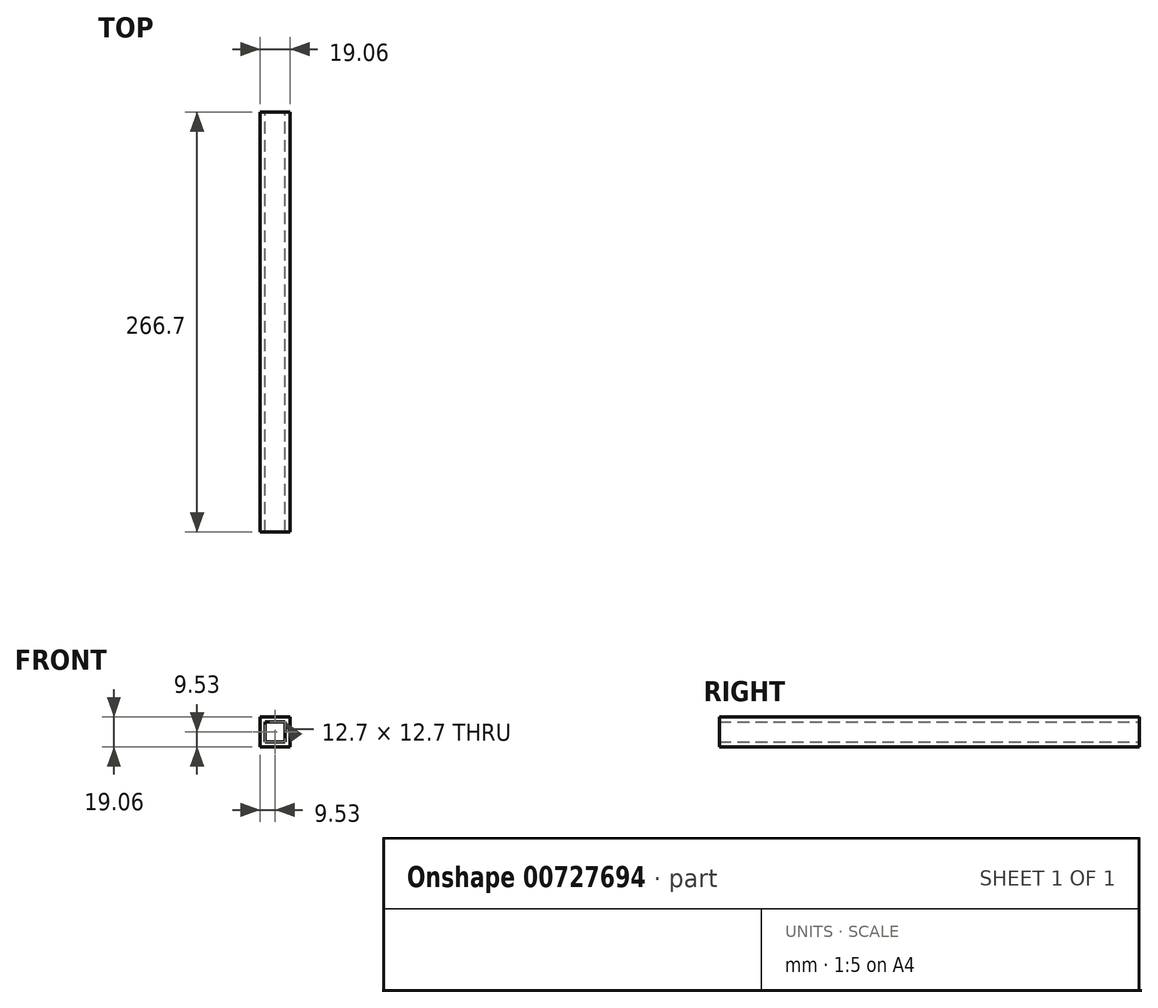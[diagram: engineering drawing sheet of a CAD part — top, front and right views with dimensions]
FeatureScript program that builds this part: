
annotation { "Feature Type Name" : "Feature", "Feature Type Description" : "" }
export const myFeature = defineFeature(function(context is Context, id is Id, definition is map)
    precondition{}
    {
        {
            var Q0;
            Q0=qCreatedBy(makeId("Front.planeOp"),FACE);
            var sketch = newSketch(context, id + "F0", { "sketchPlane" : qUnion([Q0])});
            skLineSegment(sketch, "E0.bottom", {"start": v(6.35, 6.35) * mm, "end": v(-6.35, 6.35) * mm});
            skLineSegment(sketch, "E0.top", {"start": v(6.35, -6.35) * mm, "end": v(-6.35, -6.35) * mm});
            skLineSegment(sketch, "E0.left", {"start": v(6.35, 6.35) * mm, "end": v(6.35, -6.35) * mm});
            skLineSegment(sketch, "E0.right", {"start": v(-6.35, 6.35) * mm, "end": v(-6.35, -6.35) * mm});
            skPoint(sketch, "E0.middle", {"position": v(0, 0) * mm});
            skLineSegment(sketch, "E1.0", {"start": v(9.53, -9.53) * mm, "end": v(-9.53, -9.53) * mm});
            skLineSegment(sketch, "E1.1", {"start": v(9.53, 9.53) * mm, "end": v(9.53, -9.53) * mm});
            skLineSegment(sketch, "E1.2", {"start": v(9.53, 9.53) * mm, "end": v(-9.53, 9.53) * mm});
            skLineSegment(sketch, "E1.3", {"start": v(-9.53, 9.53) * mm, "end": v(-9.53, -9.53) * mm});
            skSolve(sketch);
        }
        {
            var Q0;
            Q0=qSketchRegion(id+"F0",true);
            extrude(context, id + "F1", {"entities" : qUnion([Q0]), "depth" : 266.7 * mm, "offsetDistance" : 25.4 * mm});
        }
    });
